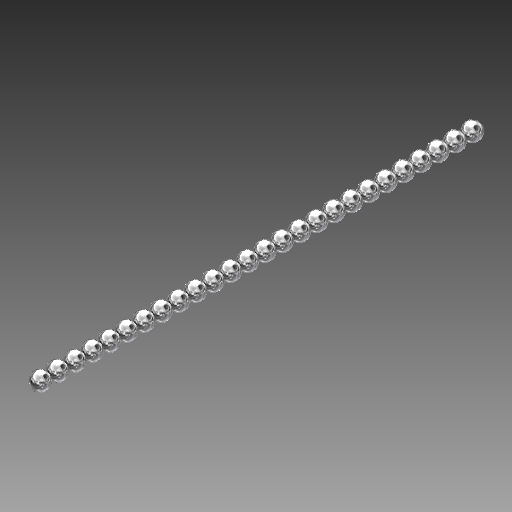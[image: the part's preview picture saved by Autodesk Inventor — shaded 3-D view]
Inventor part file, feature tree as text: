
AUTODESK INVENTOR PART (.ipt)
format: ipt  version: 2019 (Build 230136000, 136)  size: 181,248 bytes
history: native  units: mm
features: other x7, revolve x2, sketch x2, pattern_linear x1
ambient origin geometry x8: Origin, YZ Plane, XZ Plane, XY Plane, X Axis, Y Axis, Z Axis, Center Point
bodies: Solid1 (feature_tree)
feature tree (12):
  revolve  "Revolution1"  Angle=360.0deg
  revolve  "Revolution2"  [1 undecoded]
  pattern_linear  "Rectangular Pattern1"  [2 undecoded]
  other  "to_body_XY"
  other  "to_body_YZ"
  other  "to_body_ZX"
  other  "to_body_X"
  other  "to_body_Y"
  other  "to_body_Z"
  other  "to_body_Center"
  sketch  "Sketch_1"  dims[d0=360.0deg d1=360.0deg]
  sketch  "Sketch_2"  dims[d2=260.0mm d4=3.25mm d5=10.0mm d7=0.0mm]
note: 3 required parameter values undecoded (feature->parameter linkage not recoverable at this tier; creation-order binding heuristic only, values carry confidence <= 0.55)
